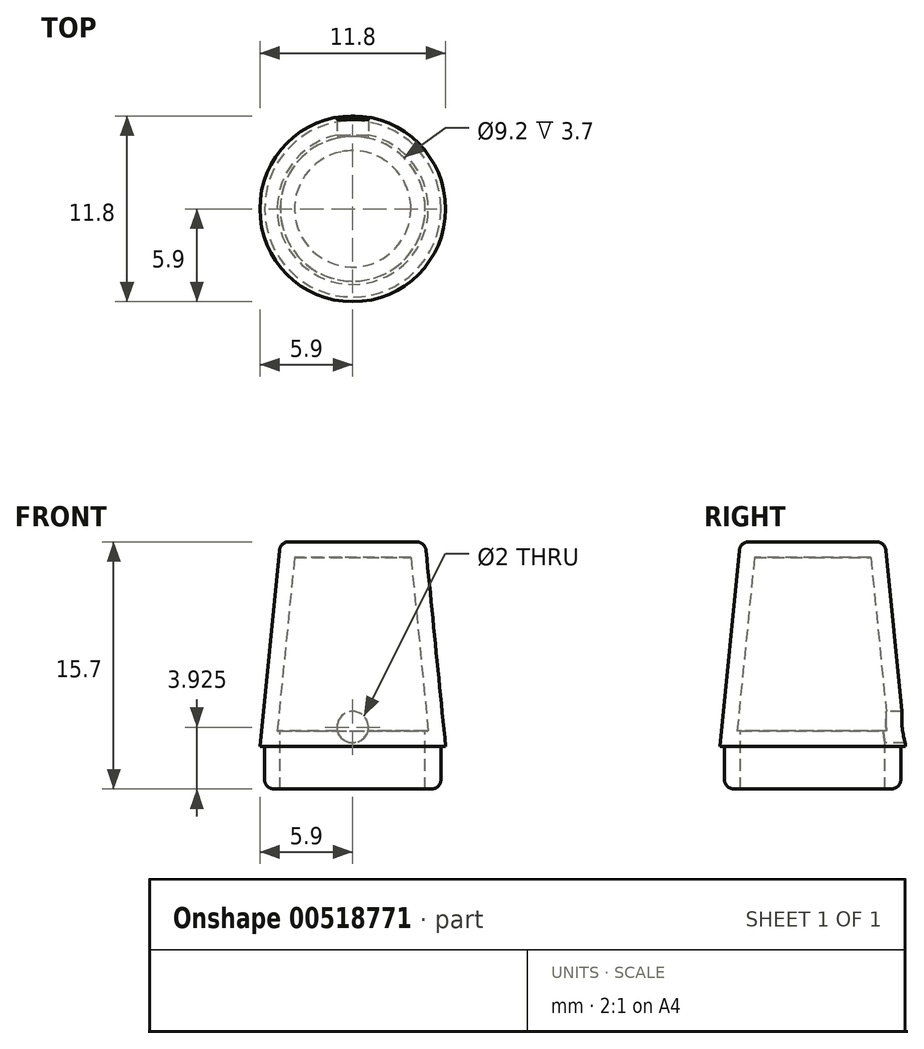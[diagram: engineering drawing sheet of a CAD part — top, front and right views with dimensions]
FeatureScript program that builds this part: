
annotation { "Feature Type Name" : "Feature", "Feature Type Description" : "" }
export const myFeature = defineFeature(function(context is Context, id is Id, definition is map)
    precondition{}
    {
        {
            var Q0;
            Q0=qCreatedBy(makeId("Front.planeOp"),FACE);
            var sketch = newSketch(context, id + "F0", { "sketchPlane" : qUnion([Q0])});
            skLineSegment(sketch, "E0", {"start": v(0, 13) * mm, "end": v(4.6, 13) * mm});
            skLineSegment(sketch, "E1", {"start": v(4.6, 13) * mm, "end": v(5.9, 0) * mm});
            skLineSegment(sketch, "E2", {"start": v(0, -2.7) * mm, "end": v(5.6, -2.7) * mm});
            skLineSegment(sketch, "E3", {"start": v(5.6, -2.7) * mm, "end": v(5.6, 0) * mm});
            skLineSegment(sketch, "E4", {"start": v(5.6, 0) * mm, "end": v(5.9, 0) * mm});
            skLineSegment(sketch, "E5", {"start": v(0, 13) * mm, "end": v(0, -2.7) * mm});
            skPoint(sketch, "E6", {"position": v(0, 1.23) * mm});
            skSolve(sketch);
        }
        {
            var Q0;
            Q0 = qSketchRegion(id + "F0", true);
            var Q1;
            Q1=sQuery(id+"F0.wireOp",EDGE,"E5");
            revolve(context, id + "F1", {"entities" : qUnion([Q0]), "axis" : qUnion([Q1]), "revolveType" : RevolveType.FULL});
        }
        {
            var Q0;
            Q0=makeQuery(id+"F1.opRevolve","SWEPT_EDGE",EDGE,{"disambiguationData":[OSD([sQuery(id+"F0.wireOp",EDGE,"E0"),sQuery(id+"F0.wireOp",EDGE,"E1")])]});
            var Q1;
            Q1=makeQuery(id+"F1.opRevolve","SWEPT_FACE",FACE,{"disambiguationData":[OSD([sQuery(id+"F0.wireOp",EDGE,"E2")])]});
            fillet(context, id + "F2", {"entities" : qUnion([Q0, Q1]), "radius" : 0.6 * mm, "tangentPropagation" : true, "allowEdgeOverflow" : false});
        }
        {
            var Q0;
            Q0=makeQuery(id+"F1.opRevolve","SWEPT_FACE",FACE,{"disambiguationData":[OSD([sQuery(id+"F0.wireOp",EDGE,"E2")])]});
            shell(context, id + "F3", {"entities" : qUnion([Q0]), "thickness" : 1 * mm});
        }
        {
            var Q0;
            Q0=sQuery(id+"F0.wireOp",VERTEX,"E6");
            var Q1;
            Q1=makeQuery(id+"F1.opRevolve","SWEPT_BODY",BODY,{"disambiguationData":[OSD([sQuery(id+"F0.wireOp",EDGE,"E0"),sQuery(id+"F0.wireOp",EDGE,"E1"),sQuery(id+"F0.wireOp",EDGE,"E2"),sQuery(id+"F0.wireOp",EDGE,"E3"),sQuery(id+"F0.wireOp",EDGE,"E4"),sQuery(id+"F0.wireOp",EDGE,"E5")])]});
            hole(context, id + "F4", {"style" : HoleStyle.SIMPLE, "endStyle" : HoleEndStyle.THROUGH, "holeDiameter" : 2 * mm, "isTappedThrough" : true, "tappedDepth" : 12 * mm, "tapClearance" : 3, "locations" : qUnion([Q0]), "scope" : qUnion([Q1])});
        }
    });
